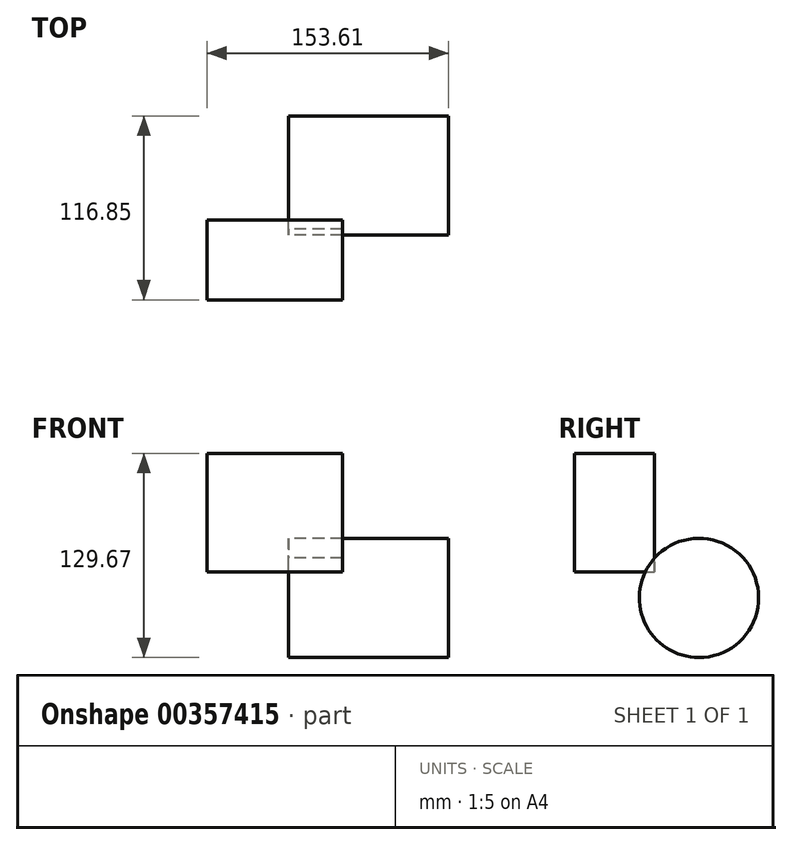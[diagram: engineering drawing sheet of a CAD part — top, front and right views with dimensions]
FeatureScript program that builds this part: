
annotation { "Feature Type Name" : "Feature", "Feature Type Description" : "" }
export const myFeature = defineFeature(function(context is Context, id is Id, definition is map)
    precondition{}
    {
        {
            var Q0;
            Q0=qCreatedBy(makeId("Front.planeOp"),FACE);
            var sketch = newSketch(context, id + "F0", { "sketchPlane" : qUnion([Q0])});
            skLineSegment(sketch, "E0.bottom", {"start": v(-52.01, 50.2) * mm, "end": v(34.12, 50.2) * mm});
            skLineSegment(sketch, "E0.top", {"start": v(-52.01, -25.01) * mm, "end": v(34.12, -25.01) * mm});
            skLineSegment(sketch, "E0.left", {"start": v(-52.01, 50.2) * mm, "end": v(-52.01, -25.01) * mm});
            skLineSegment(sketch, "E0.right", {"start": v(34.12, 50.2) * mm, "end": v(34.12, -25.01) * mm});
            skSolve(sketch);
        }
        {
            var Q0;
            Q0=makeQuery(id+"F0.imprint","IMPRINT",FACE,{"disambiguationData":[TD([[makeQuery(id+"F0.imprint","IMPRINT",EDGE,{"derivedFrom":sQuery(id+"F0.wireOp",EDGE,"E0.bottom")}),-1.0]])]});
            extrude(context, id + "F1", {"entities" : qUnion([Q0]), "depth" : 50.8 * mm});
        }
        {
            var Q0;
            Q0=qCreatedBy(makeId("Right.planeOp"),FACE);
            var sketch = newSketch(context, id + "F2", { "sketchPlane" : qUnion([Q0])});
            skCircle(sketch, "E1", {"center": v(28.18, -41.6) * mm, "radius": 37.88 * mm});
            skSolve(sketch);
        }
        {
            var Q0;
            Q0=makeQuery(id+"F2.imprint","IMPRINT",FACE,{"disambiguationData":[TD([[makeQuery(id+"F2.imprint","IMPRINT",EDGE,{"derivedFrom":sQuery(id+"F2.wireOp",EDGE,"E1")}),1.0]])]});
            extrude(context, id + "F3", {"entities" : qUnion([Q0]), "operationType" : NewBodyOperationType.ADD, "depth" : 101.6 * mm});
        }
    });
